# Revit family: Panelboard_Invicta_3_(630A-800A_Inc_125A-250A_Out)-UK-en
name_source: partatom
category: Electrical Equipment
units: mm (PartAtom-declared; Revit-internal decimal feet)

## family parameters
Cut with Voids When Loaded = No
Host = Face
Panel Configuration = Two Columns, Circuits Across
Part Type = Panelboard
Room Calculation Point = No
Round Connector Dimension = Use Diameter
Shared = No

## types (14) — shared parameters
Classification.Uniclass.Pr.Description = Control circuit device enclosures
Classification.Uniclass.Pr.Number = Pr_80_77_28_16
EF000003 - Mounting method = EV000384 - Surface mounted (plaster)
EF000007 - Colour = EV000154 - Other
EF000008 - Width = 900 mm  [stored 2.95276 ft]
EF000049 - Depth = 220 mm  [stored 0.721785 ft]
EF000118 - With mounting plate = No
EF000339 - Type of cover = EV004216 - Door
EF001062 - EMC-version = No
EF001088 - Extension possible = No
EF001134 - DIN-rail = No
EF001596 - Material housing = EV000179 - Steel
EF004462 - Type of closure = EV001412 - Cylinder
EF005474 - Degree of protection (IP) = EV006410 - IP30
EF006306 - With lock = Yes
EF015776 - Earthing terminal block = No
EF015777 - Neutral terminal block = No
EF015941 - Signal passing door = No
HG000002 - With door or cover = Yes
HG000003 - Range = Panelboards
HG000005 - Thickness = 3 mm  [stored 0.00984252 ft]
HG000017 - Distance between poles = 25 mm  [stored 0.082021 ft]
Manufacturer = Hager
Type Comments = Panelboards
zero-valued in all types: Default Elevation, EF000218 - Built-in depth, EF000266 - Number of rows, EF000332 - Built-in height, EF000846 - Built-in width, EF001131 - Internal depth

## per-type parameters (varying)
| type | EF000040 - Height | EF000116 - RAL-number | EF002950 - Width in number of modular spacings | EF006244 - Transparent cover/door | HG000004 - Manufacturer reference | Model |
| Surface mounted IP30 W900 H1250 D220 12 Modular spacings - JF80206B | 1250 mm  [stored 4.10105 ft] |  | 12 | No | JF80206B | JF80206B |
| Surface mounted IP30 W900 H1250 D220 12 Modular spacings - JF80206BG | 1250 mm  [stored 4.10105 ft] |  | 12 | Yes | JF80206BG | JF80206BG |
| Surface mounted IP30 W900 H1250 D220 12 Modular spacings - JF80404B | 1250 mm  [stored 4.10105 ft] | 7035 | 12 | No | JF80404B | JF80404B |
| Surface mounted IP30 W900 H1250 D220 12 Modular spacings - JF80404BG | 1250 mm  [stored 4.10105 ft] | 7035 | 12 | Yes | JF80404BG | JF80404BG |
| Surface mounted IP30 W900 H1250 D220 9 Modular spacings - JF60204B | 1250 mm  [stored 4.10105 ft] |  | 9 | No | JF60204B | JF60204B |
| Surface mounted IP30 W900 H1250 D220 9 Modular spacings - JF60204BG | 1250 mm  [stored 4.10105 ft] |  | 9 | Yes | JF60204BG | JF60204BG |
| Surface mounted IP30 W900 H1400 D220 18 Modular spacings - JF80210B | 1400 mm |  | 18 | No | JF80210B | JF80210B |
| Surface mounted IP30 W900 H1400 D220 18 Modular spacings - JF80210BG | 1400 mm |  | 18 | Yes | JF80210BG | JF80210BG |
| Surface mounted IP30 W900 H1400 D220 18 Modular spacings - JF80408B | 1400 mm | 7035 | 18 | No | JF80408B | JF80408B |
| Surface mounted IP30 W900 H1400 D220 18 Modular spacings - JF80408BG | 1400 mm | 7035 | 18 | Yes | JF80408BG | JF80408BG |
| Surface mounted IP30 W900 H1700 D220 27 Modular spacings - JF80414B | 1700 mm  [stored 5.57743 ft] | 7035 | 27 | No | JF80414B | JF80414B |
| Surface mounted IP30 W900 H1700 D220 27 Modular spacings - JF80414BG | 1700 mm  [stored 5.57743 ft] | 7035 | 27 | Yes | JF80414BG | JF80414BG |
| Surface mounted IP30 W900 H1700 D220 27 Modular spacings - JF80612B | 1700 mm  [stored 5.57743 ft] |  | 27 | No | JF80612B | JF80612B |
| Surface mounted IP30 W900 H1700 D220 27 Modular spacings - JF80612BG | 1700 mm  [stored 5.57743 ft] |  | 27 | Yes | JF80612BG | JF80612BG |

note: [stored X ft] marks values corroborated as IEEE doubles in the binary element streams (Revit-internal decimal feet)

## geometry (parser evidence)
native form markers: Sweep x8
no freeform markers — native parametric forms only
